# Revit family: Legrand_Transformateurs_monophasé
name_source: partatom
category: Installations électriques
revit_build: Autodesk Revit 2018 (Build: 20170223_1515(x64)
units: mm (PartAtom-declared; Revit-internal decimal feet)

## family parameters
Basée sur le plan de construction = Non
Conserver l'orientation des annotations = Non
Cote de connecteur circulaire = Utiliser le diamètre
Couper avec des vides une fois chargée = Non
Numéro OmniClass = 23.80.00.00
Partagée = Non
Point de calcul de pièce = Non
Titre OmniClass = Electric Power and Lighting
Toujours verticalement = Oui
Type d'élément = Normal

## types (4) — shared parameters
Caractéristique = Classe I - IP21 - IK08
Conditions Générale d'Utilisation = https://export.legrand.com
Fabricant = Legrand
Isolant = classe H
Modèle = Autotransformateur monophasé
Tension d'utilisation = 400-230 V ou 230-400 V par réversibilité compensée jusqu’à 16 kVA
URL = www.legrand.com

## per-type parameters (varying)
| type | 042265, 042266 | 042267 | 042268 | Poids | Section câble primaire | Section câble secondaire | Ucc (%) | diamètre de fixation | dimension A | dimension B | dimension C | fixation F | fixation G | perte totale max | perte à vide | puissance |
| Transformateur monophasé 042265 | Oui | Non | Non | 21.00 kg | 10mm² | 10 mm² | 1.7 | 7 mm  [stored 0.0229659 ft] | 250 mm  [stored 0.82021 ft] | 270 mm  [stored 0.885827 ft] | 253 mm  [stored 0.830052 ft] | 230 mm  [stored 0.754593 ft] | 91 mm  [stored 0.298556 ft] | 105 W | 55 W | 3 kVA |
| Transformateur monophasé 042267 | Non | Oui | Non | 38.00 kg | 35mm² | 35 mm² | 1.1 | 9 mm  [stored 0.0295276 ft] | 320 mm  [stored 1.04987 ft] | 330 mm | 253 mm  [stored 0.830052 ft] | 300 mm | 101 mm  [stored 0.331365 ft] | 136 W | 77 W | 6 kVA |
| Transformateur monophasé 042268 | Non | Non | Oui | 37.20 kg | 16mm² | 16 mm² | 1.3 | 9 mm  [stored 0.0295276 ft] | 300 mm | 390 mm  [stored 1.27953 ft] | 230 mm  [stored 0.754593 ft] | 280 mm  [stored 0.918635 ft] | 130 mm  [stored 0.426509 ft] | 189 W | 83 W | 8 kVA |
| Transformateur monophasé 042266 | Oui | Non | Non | 28.00 kg | 16mm² | 16 mm² | 1.1 | 7 mm  [stored 0.0229659 ft] | 250 mm  [stored 0.82021 ft] | 270 mm  [stored 0.885827 ft] | 253 mm  [stored 0.830052 ft] | 230 mm  [stored 0.754593 ft] | 130 mm  [stored 0.426509 ft] | 106 W | 66 W | 4 kVA |

note: [stored X ft] marks values corroborated as IEEE doubles in the binary element streams (Revit-internal decimal feet)
